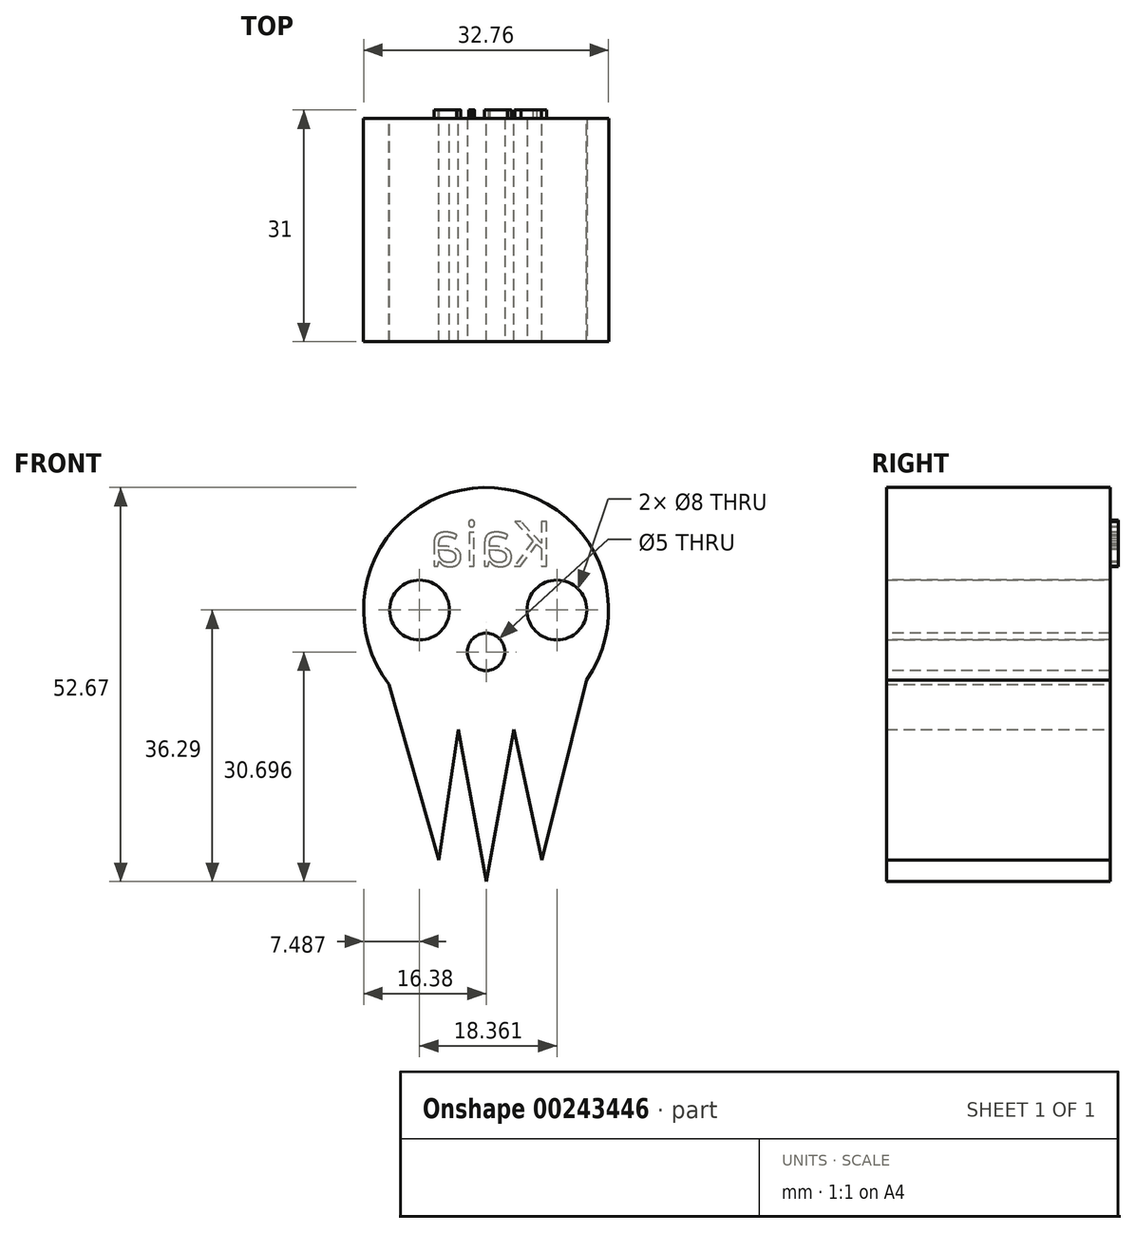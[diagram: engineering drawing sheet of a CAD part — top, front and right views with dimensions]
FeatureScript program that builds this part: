
annotation { "Feature Type Name" : "Feature", "Feature Type Description" : "" }
export const myFeature = defineFeature(function(context is Context, id is Id, definition is map)
    precondition{}
    {
        {
            var Q0;
            Q0=qCreatedBy(makeId("Front.planeOp"),FACE);
            var sketch = newSketch(context, id + "F0", { "sketchPlane" : qUnion([Q0])});
            skCircle(sketch, "E0", {"center": v(0, 0) * mm, "radius": 16.38 * mm});
            skLineSegment(sketch, "E1", {"start": v(-13, -9.97) * mm, "end": v(-6.31, -33.42) * mm});
            skLineSegment(sketch, "E2", {"start": v(-6.31, -33.42) * mm, "end": v(-3.74, -15.95) * mm});
            skLineSegment(sketch, "E3", {"start": v(-3.74, -15.95) * mm, "end": v(0, -36.3) * mm});
            skLineSegment(sketch, "E4", {"start": v(0, -36.3) * mm, "end": v(3.74, -15.95) * mm});
            skLineSegment(sketch, "E5", {"start": v(3.74, -15.95) * mm, "end": v(7.46, -33.42) * mm});
            skLineSegment(sketch, "E6", {"start": v(7.46, -33.42) * mm, "end": v(13.44, -9.37) * mm});
            skLineSegment(sketch, "E7", {"start": v(13.44, -9.37) * mm, "end": v(-13, -9.97) * mm});
            skSolve(sketch);
        }
        {
            var Q0;
            {var subQ0=sQuery(id+"F0.wireOp",EDGE,"E7");Q0=makeQuery(id+"F0.imprint","IMPRINT",FACE,{"disambiguationData":[TD([[makeQuery(id+"F0.imprint","IMPRINT",EDGE,{"derivedFrom":subQ0}),-1.0]])]});}
            var Q1;
            {var subQ0=sQuery(id+"F0.wireOp",EDGE,"E7");Q1=makeQuery(id+"F0.imprint","IMPRINT",FACE,{"disambiguationData":[TD([[makeQuery(id+"F0.imprint","IMPRINT",EDGE,{"derivedFrom":subQ0}),1.0]])]});}
            var Q2;
            {var subQ0=sQuery(id+"F0.wireOp",EDGE,"E5");Q2=makeQuery(id+"F0.imprint","IMPRINT",FACE,{"disambiguationData":[TD([[makeQuery(id+"F0.imprint","IMPRINT",EDGE,{"derivedFrom":subQ0}),1.0]])]});}
            var Q3;
            {var subQ0=sQuery(id+"F0.wireOp",EDGE,"E3");Q3=makeQuery(id+"F0.imprint","IMPRINT",FACE,{"disambiguationData":[TD([[makeQuery(id+"F0.imprint","IMPRINT",EDGE,{"derivedFrom":subQ0}),1.0]])]});}
            var Q4;
            {var subQ0=sQuery(id+"F0.wireOp",EDGE,"E1");Q4=makeQuery(id+"F0.imprint","IMPRINT",FACE,{"disambiguationData":[TD([[makeQuery(id+"F0.imprint","IMPRINT",EDGE,{"derivedFrom":subQ0}),1.0]])]});}
            extrude(context, id + "F1", {"entities" : qUnion([Q0, Q1, Q2, Q3, Q4]), "depth" : 29.9 * mm});
        }
        {
            var Q0;
            Q0=qCreatedBy(makeId("Front.planeOp"),FACE);
            var sketch = newSketch(context, id + "F2", { "sketchPlane" : qUnion([Q0])});
            skCircle(sketch, "E8", {"center": v(-8.9, 0) * mm, "radius": 4.46 * mm});
            skSolve(sketch);
        }
        {
            var Q0;
            Q0=sQuery(id+"F2.wireOp",VERTEX,"E8.center");
            var Q1;
            Q1=makeQuery(id+"F1.opExtrude","SWEPT_BODY",BODY,{"disambiguationData":[OSD([sQuery(id+"F0.wireOp",EDGE,"E0"),sQuery(id+"F0.wireOp",EDGE,"E1"),sQuery(id+"F0.wireOp",EDGE,"E2"),sQuery(id+"F0.wireOp",EDGE,"E3"),sQuery(id+"F0.wireOp",EDGE,"E4"),sQuery(id+"F0.wireOp",EDGE,"E5"),sQuery(id+"F0.wireOp",EDGE,"E6")])]});
            hole(context, id + "F3", {"style" : HoleStyle.SIMPLE, "endStyle" : HoleEndStyle.THROUGH, "oppositeDirection" : true, "holeDiameter" : 8 * mm, "tappedDepth" : 12 * mm, "tapClearance" : 3, "locations" : qUnion([Q0]), "scope" : qUnion([Q1])});
        }
        {
            var Q0;
            Q0=makeQuery(id+"F1.opExtrude","CAP_FACE",FACE,{"disambiguationData":[OSD([sQuery(id+"F0.wireOp",EDGE,"E0"),sQuery(id+"F0.wireOp",EDGE,"E1"),sQuery(id+"F0.wireOp",EDGE,"E2"),sQuery(id+"F0.wireOp",EDGE,"E3"),sQuery(id+"F0.wireOp",EDGE,"E4"),sQuery(id+"F0.wireOp",EDGE,"E5"),sQuery(id+"F0.wireOp",EDGE,"E6")])],"isStart":false});
            var sketch = newSketch(context, id + "F4", { "sketchPlane" : qUnion([Q0])});
            skCircle(sketch, "E9", {"center": v(9.47, 0) * mm, "radius": 4.46 * mm});
            skSolve(sketch);
        }
        {
            var Q0;
            Q0=sQuery(id+"F4.wireOp",VERTEX,"E9.center");
            var Q1;
            Q1=makeQuery(id+"F1.opExtrude","SWEPT_BODY",BODY,{"disambiguationData":[OSD([sQuery(id+"F0.wireOp",EDGE,"E0"),sQuery(id+"F0.wireOp",EDGE,"E1"),sQuery(id+"F0.wireOp",EDGE,"E2"),sQuery(id+"F0.wireOp",EDGE,"E3"),sQuery(id+"F0.wireOp",EDGE,"E4"),sQuery(id+"F0.wireOp",EDGE,"E5"),sQuery(id+"F0.wireOp",EDGE,"E6")])]});
            hole(context, id + "F5", {"style" : HoleStyle.SIMPLE, "endStyle" : HoleEndStyle.THROUGH, "holeDiameter" : 8 * mm, "tappedDepth" : 12 * mm, "tapClearance" : 3, "locations" : qUnion([Q0]), "scope" : qUnion([Q1])});
        }
        {
            var Q0;
            Q0=makeQuery(id+"F1.opExtrude","CAP_FACE",FACE,{"disambiguationData":[OSD([sQuery(id+"F0.wireOp",EDGE,"E0"),sQuery(id+"F0.wireOp",EDGE,"E1"),sQuery(id+"F0.wireOp",EDGE,"E2"),sQuery(id+"F0.wireOp",EDGE,"E3"),sQuery(id+"F0.wireOp",EDGE,"E4"),sQuery(id+"F0.wireOp",EDGE,"E5"),sQuery(id+"F0.wireOp",EDGE,"E6")])],"isStart":false});
            var sketch = newSketch(context, id + "F6", { "sketchPlane" : qUnion([Q0])});
            skCircle(sketch, "E10", {"center": v(0, -5.6) * mm, "radius": 2.6 * mm});
            skSolve(sketch);
        }
        {
            var Q0;
            Q0=sQuery(id+"F6.wireOp",VERTEX,"E10.center");
            var Q1;
            Q1=makeQuery(id+"F1.opExtrude","SWEPT_BODY",BODY,{"disambiguationData":[OSD([sQuery(id+"F0.wireOp",EDGE,"E0"),sQuery(id+"F0.wireOp",EDGE,"E1"),sQuery(id+"F0.wireOp",EDGE,"E2"),sQuery(id+"F0.wireOp",EDGE,"E3"),sQuery(id+"F0.wireOp",EDGE,"E4"),sQuery(id+"F0.wireOp",EDGE,"E5"),sQuery(id+"F0.wireOp",EDGE,"E6")])]});
            hole(context, id + "F7", {"style" : HoleStyle.SIMPLE, "endStyle" : HoleEndStyle.THROUGH, "holeDiameter" : 5 * mm, "tappedDepth" : 12 * mm, "tapClearance" : 3, "locations" : qUnion([Q0]), "scope" : qUnion([Q1])});
        }
        {
            var Q0;
            Q0=makeQuery(id+"F1.opExtrude","CAP_FACE",FACE,{"disambiguationData":[OSD([sQuery(id+"F0.wireOp",EDGE,"E0"),sQuery(id+"F0.wireOp",EDGE,"E1"),sQuery(id+"F0.wireOp",EDGE,"E2"),sQuery(id+"F0.wireOp",EDGE,"E3"),sQuery(id+"F0.wireOp",EDGE,"E4"),sQuery(id+"F0.wireOp",EDGE,"E5"),sQuery(id+"F0.wireOp",EDGE,"E6")])],"isStart":true});
            var sketch = newSketch(context, id + "F8", { "sketchPlane" : qUnion([Q0])});
            skText(sketch, "E11", { "text": "Kaia", "fontName": "OpenSans-Regular.ttf"});
            const initialGuessF8  = {"E11": [-0.0089, 0.00588, 1, 0, 0.00602]};
            skSetInitialGuess(sketch, initialGuessF8);
            skSolve(sketch);
        }
        {
            var Q0;
            Q0 = qSketchRegion(id + "F8", true);
            extrude(context, id + "F9", {"entities" : qUnion([Q0]), "operationType" : NewBodyOperationType.ADD, "depth" : 1.1 * mm});
        }
    });
